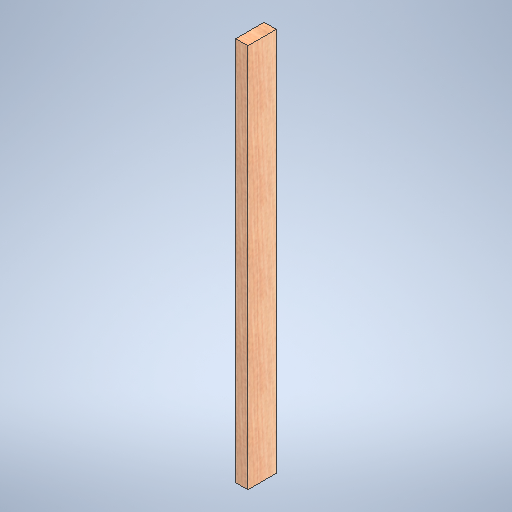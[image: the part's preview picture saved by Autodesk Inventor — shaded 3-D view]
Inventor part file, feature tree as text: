
AUTODESK INVENTOR PART (.ipt)
format: ipt  version: 2025 (Build 290162010, 162A)  size: 307,712 bytes
history: native  units: in
note: dims shown in document units (in); Inventor stores cm internally (conversion verified against a paired STEP export)
features: extrude x1, sketch x1
ambient origin geometry x8: Origin, YZ Plane, XZ Plane, XY Plane, X Axis, Y Axis, Z Axis, Center Point
bodies: Solid1 (feature_tree)
feature tree (2):
  extrude  "Extrusion1"  Depth=1.5in
  sketch  "Sketch1"  dims[d0=3.5in d1=1.5in d2=47.25in d3=0.0in]
